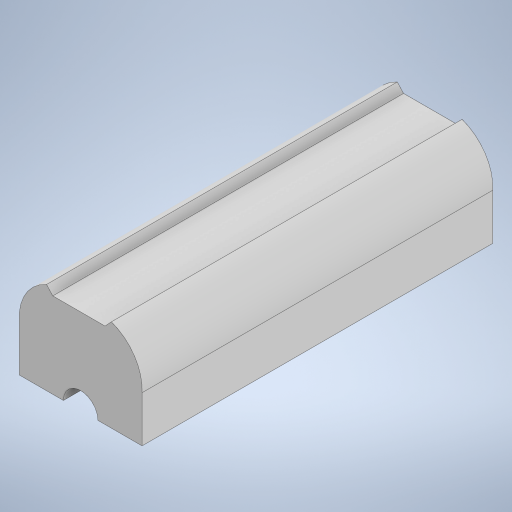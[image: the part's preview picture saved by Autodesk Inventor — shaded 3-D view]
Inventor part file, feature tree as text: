
AUTODESK INVENTOR PART (.ipt)
format: ipt  version: 2023 (Build 270158000, 158)  size: 240,640 bytes
history: native  units: in
note: dims shown in document units (in); Inventor stores cm internally (conversion verified against a paired STEP export)
features: extrude x1, sketch x1
ambient origin geometry x8: Origin, YZ Plane, XZ Plane, XY Plane, X Axis, Y Axis, Z Axis, Center Point
bodies: Solid1 (feature_tree)
feature tree (2):
  extrude  "Extrusion1"  Depth=1.1811in
  sketch  "Sketch1"  dims[d0=1.5748in d1=1.1811in d2=1.5748in d3=1.1811in d4=1.1811in d5=2.3622in d7=0.2362in d9=0.7874in d10=0.8858in d11=9.0in d12=0.0in d13=0.0344in d14=0.0344in]
